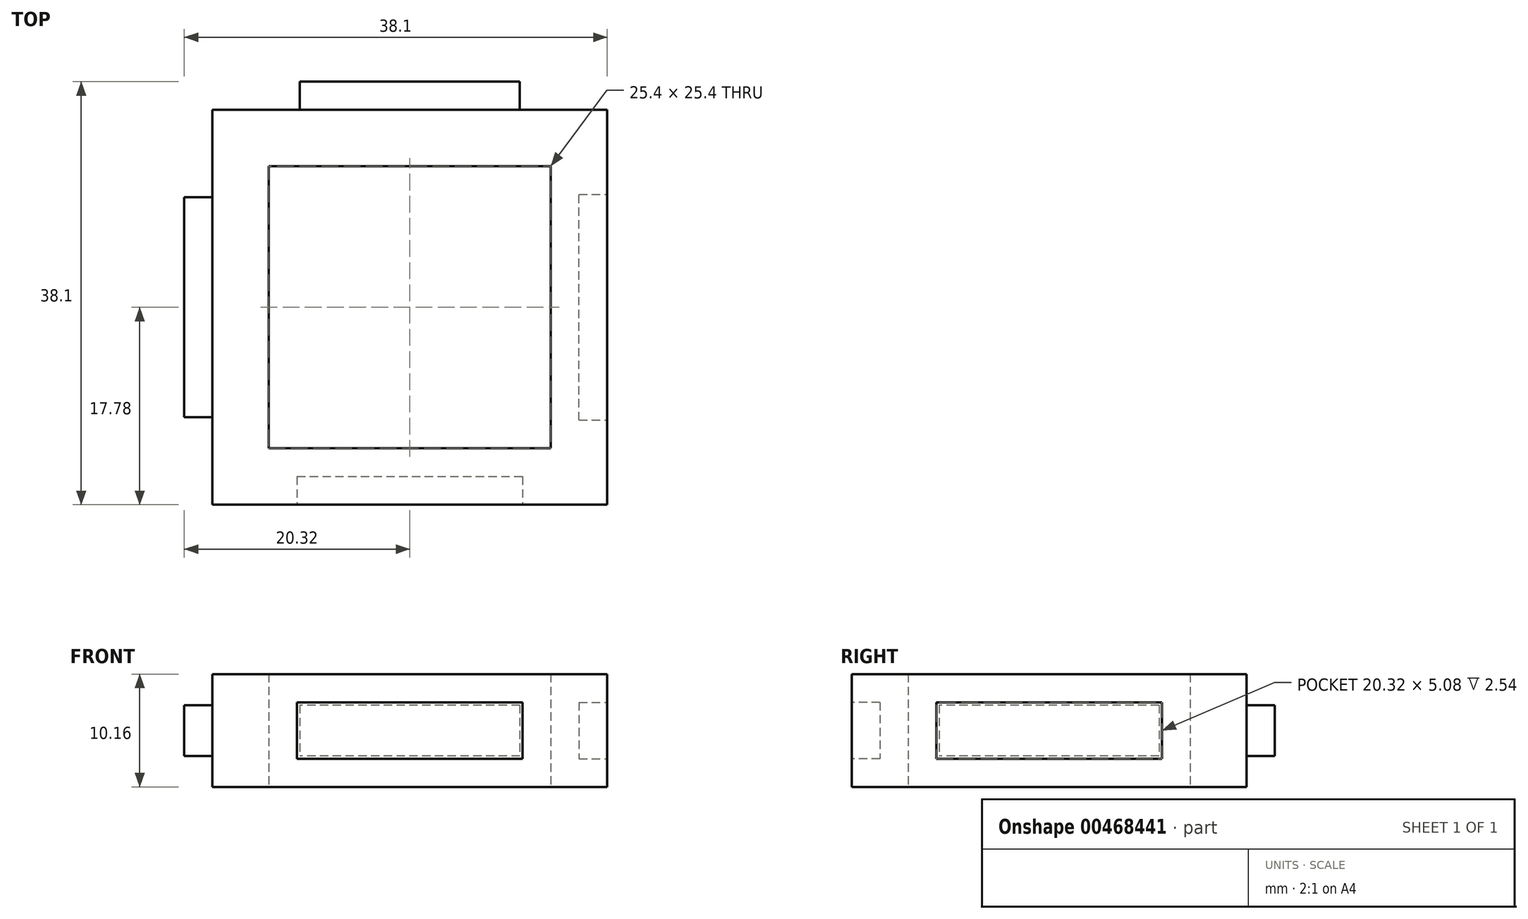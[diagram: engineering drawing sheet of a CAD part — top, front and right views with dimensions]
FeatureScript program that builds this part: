
annotation { "Feature Type Name" : "Feature", "Feature Type Description" : "" }
export const myFeature = defineFeature(function(context is Context, id is Id, definition is map)
    precondition{}
    {
        {
            var Q0;
            Q0=qCreatedBy(makeId("Top.planeOp"),FACE);
            var sketch = newSketch(context, id + "F0", { "sketchPlane" : qUnion([Q0])});
            skLineSegment(sketch, "E0.bottom", {"start": v(-17.78, 17.78) * mm, "end": v(17.78, 17.78) * mm});
            skLineSegment(sketch, "E0.top", {"start": v(-17.78, -17.78) * mm, "end": v(17.78, -17.78) * mm});
            skLineSegment(sketch, "E0.left", {"start": v(-17.78, 17.78) * mm, "end": v(-17.78, -17.78) * mm});
            skLineSegment(sketch, "E0.right", {"start": v(17.78, 17.78) * mm, "end": v(17.78, -17.78) * mm});
            skLineSegment(sketch, "E1.bottom", {"start": v(-12.7, 12.7) * mm, "end": v(12.7, 12.7) * mm});
            skLineSegment(sketch, "E1.top", {"start": v(-12.7, -12.7) * mm, "end": v(12.7, -12.7) * mm});
            skLineSegment(sketch, "E1.left", {"start": v(-12.7, 12.7) * mm, "end": v(-12.7, -12.7) * mm});
            skLineSegment(sketch, "E1.right", {"start": v(12.7, 12.7) * mm, "end": v(12.7, -12.7) * mm});
            skSolve(sketch);
        }
        {
            var Q0;
            Q0=qSketchRegion(id+"F0",true);
            extrude(context, id + "F1", {"entities" : qUnion([Q0]), "endBound" : BoundingType.SYMMETRIC, "depth" : 10.16 * mm});
        }
        {
            var Q0;
            Q0=makeQuery(id+"F1.opExtrude","SWEPT_FACE",FACE,{"disambiguationData":[OSD([sQuery(id+"F0.wireOp",EDGE,"E0.bottom")])]});
            var sketch = newSketch(context, id + "F2", { "sketchPlane" : qUnion([Q0])});
            skLineSegment(sketch, "E2.bottom", {"start": v(-9.9, 2.29) * mm, "end": v(9.9, 2.29) * mm});
            skLineSegment(sketch, "E2.top", {"start": v(-9.9, -2.29) * mm, "end": v(9.9, -2.29) * mm});
            skLineSegment(sketch, "E2.left", {"start": v(-9.9, 2.29) * mm, "end": v(-9.9, -2.29) * mm});
            skLineSegment(sketch, "E2.right", {"start": v(9.9, 2.29) * mm, "end": v(9.9, -2.29) * mm});
            skSolve(sketch);
        }
        {
            var Q0;
            Q0=qSketchRegion(id+"F2",true);
            extrude(context, id + "F3", {"entities" : qUnion([Q0]), "operationType" : NewBodyOperationType.ADD, "depth" : 2.54 * mm});
        }
        {
            var Q0;
            Q0=makeQuery(id+"F1.opExtrude","SWEPT_FACE",FACE,{"disambiguationData":[OSD([sQuery(id+"F0.wireOp",EDGE,"E0.left")])]});
            var sketch = newSketch(context, id + "F4", { "sketchPlane" : qUnion([Q0])});
            skLineSegment(sketch, "E3.bottom", {"start": v(-9.9, 2.29) * mm, "end": v(9.9, 2.29) * mm});
            skLineSegment(sketch, "E3.top", {"start": v(-9.9, -2.29) * mm, "end": v(9.9, -2.29) * mm});
            skLineSegment(sketch, "E3.left", {"start": v(-9.9, 2.29) * mm, "end": v(-9.9, -2.29) * mm});
            skLineSegment(sketch, "E3.right", {"start": v(9.9, 2.29) * mm, "end": v(9.9, -2.29) * mm});
            skSolve(sketch);
        }
        {
            var Q0;
            Q0=qSketchRegion(id+"F4",true);
            extrude(context, id + "F5", {"entities" : qUnion([Q0]), "operationType" : NewBodyOperationType.ADD, "depth" : 2.54 * mm});
        }
        {
            var Q0;
            Q0=makeQuery(id+"F1.opExtrude","SWEPT_FACE",FACE,{"disambiguationData":[OSD([sQuery(id+"F0.wireOp",EDGE,"E0.top")])]});
            var sketch = newSketch(context, id + "F6", { "sketchPlane" : qUnion([Q0])});
            skLineSegment(sketch, "E4.bottom", {"start": v(-10.16, 2.54) * mm, "end": v(10.16, 2.54) * mm});
            skLineSegment(sketch, "E4.top", {"start": v(-10.16, -2.54) * mm, "end": v(10.16, -2.54) * mm});
            skLineSegment(sketch, "E4.left", {"start": v(-10.16, 2.54) * mm, "end": v(-10.16, -2.54) * mm});
            skLineSegment(sketch, "E4.right", {"start": v(10.16, 2.54) * mm, "end": v(10.16, -2.54) * mm});
            skSolve(sketch);
        }
        {
            var Q0;
            Q0=qSketchRegion(id+"F6",true);
            extrude(context, id + "F7", {"entities" : qUnion([Q0]), "operationType" : NewBodyOperationType.REMOVE, "oppositeDirection" : true, "depth" : 2.54 * mm});
        }
        {
            var Q0;
            Q0=makeQuery(id+"F1.opExtrude","SWEPT_FACE",FACE,{"disambiguationData":[OSD([sQuery(id+"F0.wireOp",EDGE,"E0.right")])]});
            var sketch = newSketch(context, id + "F8", { "sketchPlane" : qUnion([Q0])});
            skLineSegment(sketch, "E5.bottom", {"start": v(-10.16, 2.54) * mm, "end": v(10.16, 2.54) * mm});
            skLineSegment(sketch, "E5.top", {"start": v(-10.16, -2.54) * mm, "end": v(10.16, -2.54) * mm});
            skLineSegment(sketch, "E5.left", {"start": v(-10.16, 2.54) * mm, "end": v(-10.16, -2.54) * mm});
            skLineSegment(sketch, "E5.right", {"start": v(10.16, 2.54) * mm, "end": v(10.16, -2.54) * mm});
            skSolve(sketch);
        }
        {
            var Q0;
            Q0=qSketchRegion(id+"F8",true);
            extrude(context, id + "F9", {"entities" : qUnion([Q0]), "operationType" : NewBodyOperationType.REMOVE, "oppositeDirection" : true, "depth" : 2.54 * mm});
        }
    });
